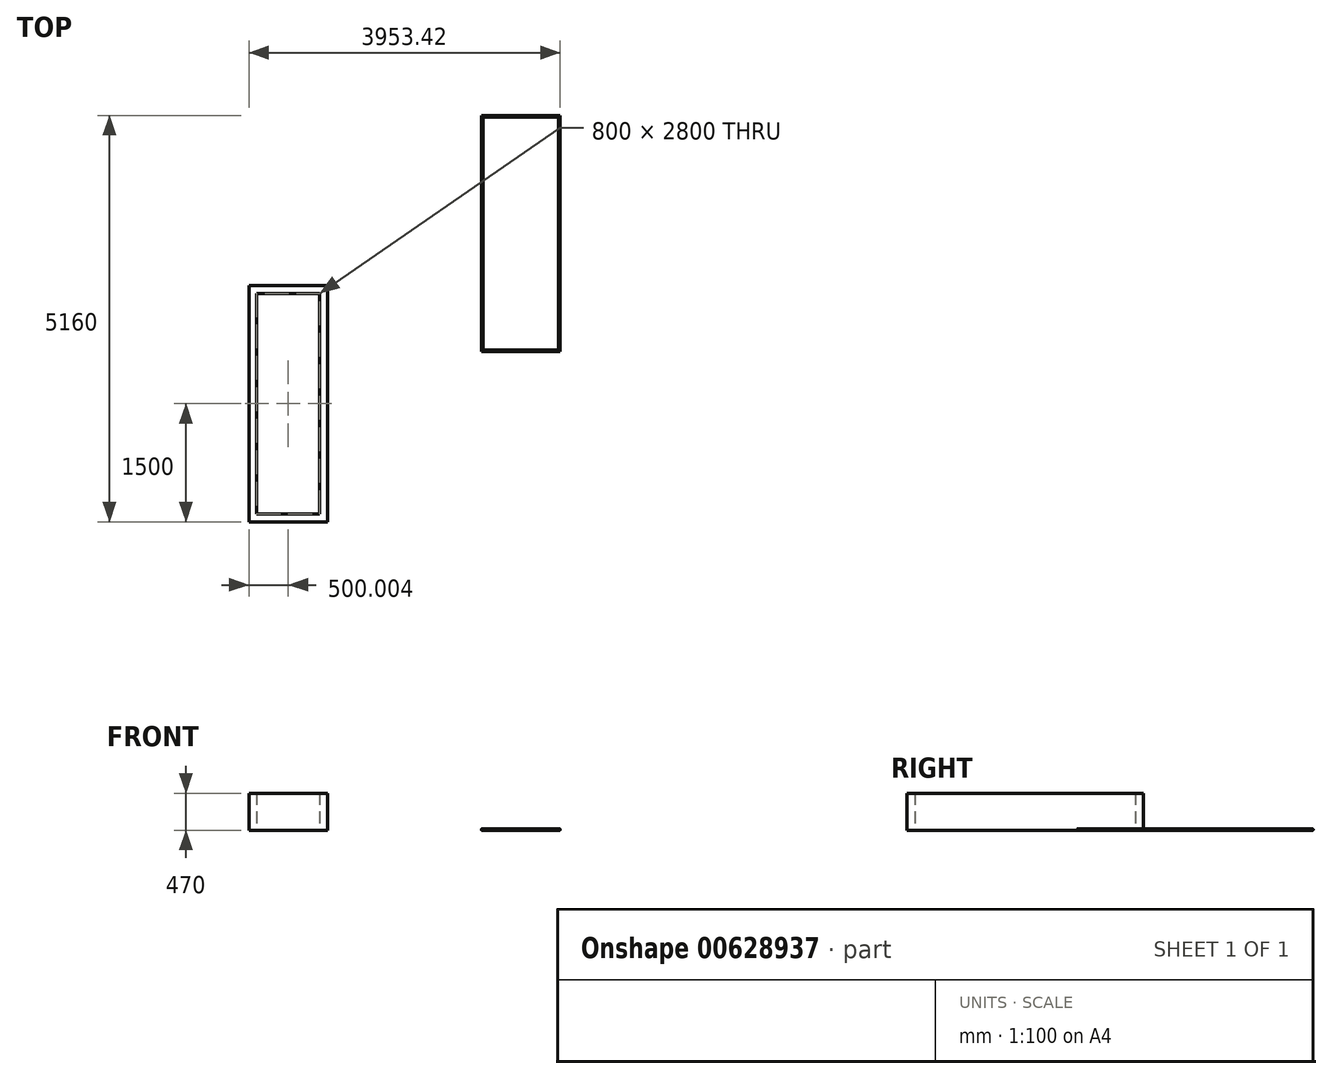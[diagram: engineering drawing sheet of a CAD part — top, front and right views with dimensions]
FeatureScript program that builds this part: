
annotation { "Feature Type Name" : "Feature", "Feature Type Description" : "" }
export const myFeature = defineFeature(function(context is Context, id is Id, definition is map)
    precondition{}
    {
        {
            var Q0;
            Q0=qCreatedBy(makeId("Top.planeOp"),FACE);
            var sketch = newSketch(context, id + "F0", { "sketchPlane" : qUnion([Q0])});
            skLineSegment(sketch, "E0", {"start": v(-55.9, 2919.52) * mm, "end": v(-55.9, -80.48) * mm});
            skLineSegment(sketch, "E1", {"start": v(-55.9, -80.48) * mm, "end": v(944.1, -80.48) * mm});
            skLineSegment(sketch, "E2", {"start": v(944.1, -80.48) * mm, "end": v(944.1, 2919.52) * mm});
            skLineSegment(sketch, "E3", {"start": v(944.1, 2919.52) * mm, "end": v(-55.9, 2919.52) * mm});
            skLineSegment(sketch, "E4.0", {"start": v(844.1, 19.52) * mm, "end": v(844.1, 2819.52) * mm});
            skLineSegment(sketch, "E4.1", {"start": v(44.1, 19.52) * mm, "end": v(844.1, 19.52) * mm});
            skLineSegment(sketch, "E4.2", {"start": v(44.1, 2819.52) * mm, "end": v(44.1, 19.52) * mm});
            skLineSegment(sketch, "E4.3", {"start": v(844.1, 2819.52) * mm, "end": v(44.1, 2819.52) * mm});
            skLineSegment(sketch, "E5", {"start": v(2897.52, 5079.52) * mm, "end": v(2897.52, 2079.52) * mm});
            skLineSegment(sketch, "E6", {"start": v(2897.52, 2079.52) * mm, "end": v(3897.52, 2079.52) * mm});
            skLineSegment(sketch, "E7", {"start": v(3897.52, 2079.52) * mm, "end": v(3897.52, 5079.52) * mm});
            skLineSegment(sketch, "E8", {"start": v(3897.52, 5079.52) * mm, "end": v(2897.52, 5079.52) * mm});
            skLineSegment(sketch, "E9.0", {"start": v(3877.52, 2099.52) * mm, "end": v(3877.52, 5059.52) * mm});
            skLineSegment(sketch, "E9.1", {"start": v(2917.52, 2099.52) * mm, "end": v(3877.52, 2099.52) * mm});
            skLineSegment(sketch, "E9.2", {"start": v(2917.52, 5059.52) * mm, "end": v(2917.52, 2099.52) * mm});
            skLineSegment(sketch, "E9.3", {"start": v(3877.52, 5059.52) * mm, "end": v(2917.52, 5059.52) * mm});
            skSolve(sketch);
        }
        {
            var Q0;
            Q0=makeQuery(id+"F0.imprint","IMPRINT",FACE,{"disambiguationData":[TD([[makeQuery(id+"F0.imprint","IMPRINT",EDGE,{"derivedFrom":sQuery(id+"F0.wireOp",EDGE,"E0")}),1.0]])]});
            extrude(context, id + "F1", {"entities" : qUnion([Q0]), "depth" : 470 * mm, "offsetDistance" : 25 * mm});
        }
        {
            var Q0;
            Q0=makeQuery(id+"F0.imprint","IMPRINT",FACE,{"disambiguationData":[TD([[makeQuery(id+"F0.imprint","IMPRINT",EDGE,{"derivedFrom":sQuery(id+"F0.wireOp",EDGE,"E5")}),1.0]])]});
            extrude(context, id + "F2", {"entities" : qUnion([Q0]), "depth" : 20 * mm, "offsetDistance" : 25 * mm});
        }
        {
            var Q0;
            Q0=makeQuery(id+"F2.opExtrude","CAP_FACE",FACE,{"disambiguationData":[OSD([sQuery(id+"F0.wireOp",EDGE,"E5"),sQuery(id+"F0.wireOp",EDGE,"E6"),sQuery(id+"F0.wireOp",EDGE,"E7"),sQuery(id+"F0.wireOp",EDGE,"E8"),sQuery(id+"F0.wireOp",EDGE,"E9.0"),sQuery(id+"F0.wireOp",EDGE,"E9.1"),sQuery(id+"F0.wireOp",EDGE,"E9.2"),sQuery(id+"F0.wireOp",EDGE,"E9.3")])],"isStart":true});
            var Q1;
            Q1=makeQuery(id+"F2.opExtrude","CAP_FACE",FACE,{"disambiguationData":[OSD([sQuery(id+"F0.wireOp",EDGE,"E5"),sQuery(id+"F0.wireOp",EDGE,"E6"),sQuery(id+"F0.wireOp",EDGE,"E7"),sQuery(id+"F0.wireOp",EDGE,"E8"),sQuery(id+"F0.wireOp",EDGE,"E9.0"),sQuery(id+"F0.wireOp",EDGE,"E9.1"),sQuery(id+"F0.wireOp",EDGE,"E9.2"),sQuery(id+"F0.wireOp",EDGE,"E9.3")])],"isStart":false});
            fillet(context, id + "F3", {"entities" : qUnion([Q0, Q1]), "radius" : 10 * mm, "tangentPropagation" : true, "allowEdgeOverflow" : false});
        }
    });
